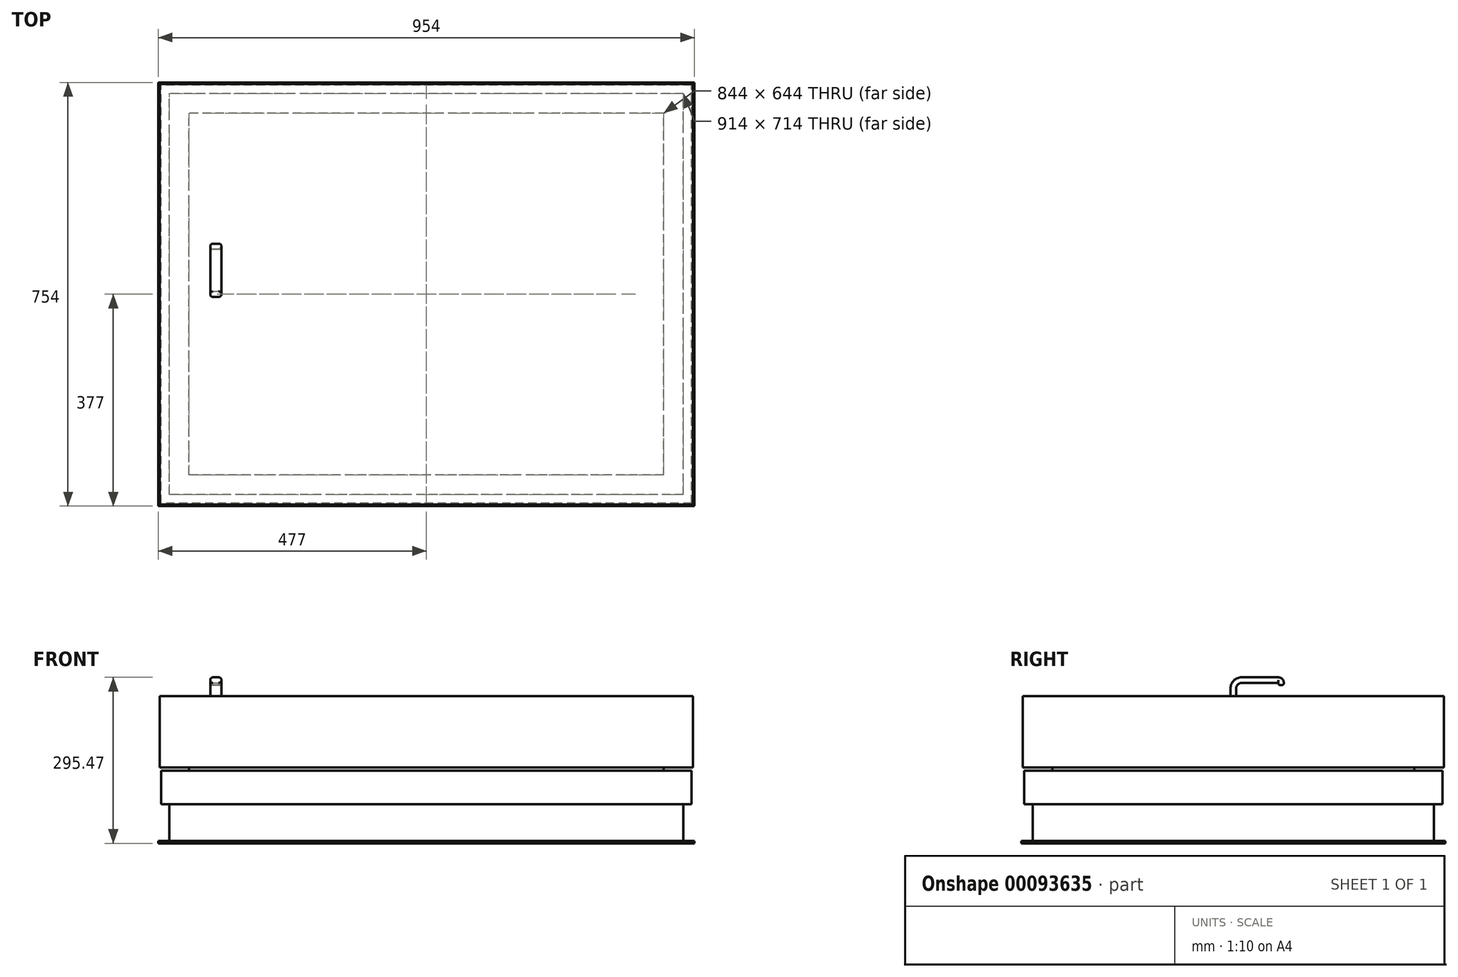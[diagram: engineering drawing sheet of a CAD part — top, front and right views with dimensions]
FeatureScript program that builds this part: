
annotation { "Feature Type Name" : "Feature", "Feature Type Description" : "" }
export const myFeature = defineFeature(function(context is Context, id is Id, definition is map)
    precondition{}
    {
        {
            var Q0;
            Q0=qCreatedBy(makeId("Front.planeOp"),FACE);
            var sketch = newSketch(context, id + "F0", { "sketchPlane" : qUnion([Q0])});
            skLineSegment(sketch, "E0.bottom", {"start": v(-477, -131) * mm, "end": v(477, -131) * mm});
            skLineSegment(sketch, "E0.top", {"start": v(-474.5, 131) * mm, "end": v(474.5, 131) * mm});
            skLineSegment(sketch, "E0.left", {"start": v(-477, -131) * mm, "end": v(-477, -127) * mm});
            skLineSegment(sketch, "E0.right", {"start": v(477, -131) * mm, "end": v(477, -127) * mm});
            skPoint(sketch, "E0.middle", {"position": v(0, 0) * mm});
            skLineSegment(sketch, "E1", {"start": v(477, -127) * mm, "end": v(457, -127) * mm});
            skLineSegment(sketch, "E2", {"start": v(457, -127) * mm, "end": v(457, -61.5) * mm});
            skLineSegment(sketch, "E3", {"start": v(457, -61.5) * mm, "end": v(472, -61.5) * mm});
            skLineSegment(sketch, "E4", {"start": v(472, -61.5) * mm, "end": v(472, -1.5) * mm});
            skLineSegment(sketch, "E5", {"start": v(472, -1.5) * mm, "end": v(422, -1.5) * mm});
            skLineSegment(sketch, "E6", {"start": v(422, -1.5) * mm, "end": v(422, 4) * mm});
            skLineSegment(sketch, "E7", {"start": v(422, 4) * mm, "end": v(474.5, 4) * mm});
            skLineSegment(sketch, "E8", {"start": v(474.5, 4) * mm, "end": v(474.5, 131) * mm});
            skPoint(sketch, "E9.orphan", {"position": v(477, 131) * mm});
            skLineSegment(sketch, "E10.MirrorCS", {"start": v(-474.5, 4) * mm, "end": v(-474.5, 131) * mm});
            skLineSegment(sketch, "E11.MirrorCS", {"start": v(-422, 4) * mm, "end": v(-474.5, 4) * mm});
            skLineSegment(sketch, "E12.MirrorCS", {"start": v(-472, -1.5) * mm, "end": v(-422, -1.5) * mm});
            skLineSegment(sketch, "E13.MirrorCS", {"start": v(-472, -61.5) * mm, "end": v(-472, -1.5) * mm});
            skLineSegment(sketch, "E14.MirrorCS", {"start": v(-457, -127) * mm, "end": v(-457, -61.5) * mm});
            skLineSegment(sketch, "E15.MirrorCS", {"start": v(-457, -61.5) * mm, "end": v(-472, -61.5) * mm});
            skLineSegment(sketch, "E16.MirrorCS", {"start": v(-422, -1.5) * mm, "end": v(-422, 4) * mm});
            skLineSegment(sketch, "E17.MirrorCS", {"start": v(-477, -127) * mm, "end": v(-457, -127) * mm});
            skPoint(sketch, "E18.orphan", {"position": v(-477, 131) * mm});
            skSolve(sketch);
        }
        {
            var Q0;
            Q0 = qSketchRegion(id + "F0", true);
            extrude(context, id + "F1", {"entities" : qUnion([Q0]), "depth" : 754 * mm});
        }
        {
            var Q0;
            Q0=makeQuery(id+"F1.opExtrude","SWEPT_FACE",FACE,{"disambiguationData":[OSD([sQuery(id+"F0.wireOp",EDGE,"E10.MirrorCS")])]});
            var sketch = newSketch(context, id + "F2", { "sketchPlane" : qUnion([Q0])});
            skLineSegment(sketch, "E19.right", {"start": v(754, -131) * mm, "end": v(754, -127) * mm});
            skPoint(sketch, "E19.middle", {"position": v(377, 0) * mm});
            skLineSegment(sketch, "E20", {"start": v(754, -127) * mm, "end": v(734, -127) * mm});
            skLineSegment(sketch, "E21", {"start": v(734, -127) * mm, "end": v(734, -61.5) * mm});
            skLineSegment(sketch, "E22", {"start": v(734, -61.5) * mm, "end": v(749, -61.5) * mm});
            skLineSegment(sketch, "E23", {"start": v(749, -61.5) * mm, "end": v(749, -1.5) * mm});
            skLineSegment(sketch, "E24", {"start": v(749, -1.5) * mm, "end": v(699, -1.5) * mm});
            skLineSegment(sketch, "E25", {"start": v(699, -1.5) * mm, "end": v(699, 4) * mm});
            skLineSegment(sketch, "E26", {"start": v(699, 4) * mm, "end": v(751.5, 4) * mm});
            skLineSegment(sketch, "E27", {"start": v(751.5, 4) * mm, "end": v(751.5, 131) * mm});
            skPoint(sketch, "E28.orphan", {"position": v(754, 131) * mm});
            skPoint(sketch, "E29.orphan", {"position": v(0, 131) * mm});
            skLineSegment(sketch, "E30", {"start": v(377, -206.18) * mm, "end": v(377, 179.39) * mm, "construction": true});
            skPoint(sketch, "E30.startSnap0", {"position": v(377, -131) * mm});
            skPoint(sketch, "E30.endSnap0", {"position": v(377, 131) * mm});
            skLineSegment(sketch, "E31.MirrorCS", {"start": v(2.5, 4) * mm, "end": v(2.5, 131) * mm});
            skLineSegment(sketch, "E32.MirrorCS", {"start": v(55, 4) * mm, "end": v(2.5, 4) * mm});
            skLineSegment(sketch, "E33.MirrorCS", {"start": v(55, -1.5) * mm, "end": v(55, 4) * mm});
            skLineSegment(sketch, "E34.MirrorCS", {"start": v(5, -1.5) * mm, "end": v(55, -1.5) * mm});
            skLineSegment(sketch, "E35.MirrorCS", {"start": v(5, -61.5) * mm, "end": v(5, -1.5) * mm});
            skLineSegment(sketch, "E36.MirrorCS", {"start": v(20, -127) * mm, "end": v(20, -61.5) * mm});
            skLineSegment(sketch, "E37.MirrorCS", {"start": v(20, -61.5) * mm, "end": v(5, -61.5) * mm});
            skLineSegment(sketch, "E38.MirrorCS", {"start": v(0, -127) * mm, "end": v(20, -127) * mm});
            skLineSegment(sketch, "E39.MirrorCS", {"start": v(0, -131) * mm, "end": v(0, -127) * mm});
            skLineSegment(sketch, "E40", {"start": v(751.5, 131) * mm, "end": v(774.44, 131) * mm});
            skLineSegment(sketch, "E41", {"start": v(774.44, 131) * mm, "end": v(765.52, -131) * mm});
            skLineSegment(sketch, "E42", {"start": v(765.52, -131) * mm, "end": v(754, -131) * mm});
            skLineSegment(sketch, "E43.MirrorCS", {"start": v(-20.44, 131) * mm, "end": v(-11.52, -131) * mm});
            skLineSegment(sketch, "E44.MirrorCS", {"start": v(-11.52, -131) * mm, "end": v(0, -131) * mm});
            skLineSegment(sketch, "E45.MirrorCS", {"start": v(2.5, 131) * mm, "end": v(-20.44, 131) * mm});
            skSolve(sketch);
        }
        {
            var Q0;
            Q0 = qSketchRegion(id + "F2", true);
            extrude(context, id + "F3", {"entities" : qUnion([Q0]), "operationType" : NewBodyOperationType.REMOVE, "oppositeDirection" : true, "depth" : 999 * mm});
        }
        {
            var Q0;
            Q0=makeQuery(id+"F1.opExtrude","SWEPT_FACE",FACE,{"disambiguationData":[OSD([sQuery(id+"F0.wireOp",EDGE,"E10.MirrorCS")])]});
            cPlane(context, id + "F4", {"entities" : qUnion([Q0]), "cplaneType" : CPlaneType.OFFSET, "offset" : 100 * mm, "oppositeDirection" : true, "width" : 150 * mm, "height" : 150 * mm});
        }
        {
            var Q0;
            Q0=qCreatedBy(id+"F4.planeOp",FACE);
            var sketch = newSketch(context, id + "F5", { "sketchPlane" : qUnion([Q0])});
            skLineSegment(sketch, "E46", {"start": v(377, 131) * mm, "end": v(377, 144.47) * mm});
            skLineSegment(sketch, "E47", {"start": v(362, 159.47) * mm, "end": v(297, 159.47) * mm});
            skLineSegment(sketch, "E48", {"start": v(292, 154.47) * mm, "end": v(292, 150.87) * mm});
            skPoint(sketch, "E49.visualSharp", {"position": v(377, 159.47) * mm});
            skArc(sketch, "E49.filletArc", {"start": v(377, 144.47) * mm, "mid": v(372.6, 155.08) * mm, "end": v(362, 159.47) * mm});
            skPoint(sketch, "E50.visualSharp", {"position": v(292, 159.47) * mm});
            skArc(sketch, "E50.filletArc", {"start": v(297, 159.47) * mm, "mid": v(293.46, 158) * mm, "end": v(292, 154.47) * mm});
            skSolve(sketch);
        }
        {
            var Q0;
            Q0=makeQuery(id+"F1.opExtrude","SWEPT_FACE",FACE,{"disambiguationData":[OSD([sQuery(id+"F0.wireOp",EDGE,"E0.top")])]});
            var sketch = newSketch(context, id + "F6", { "sketchPlane" : qUnion([Q0])});
            skPoint(sketch, "E51.0", {"position": v(-374.5, -377) * mm});
            skLineSegment(sketch, "E52.bottom", {"start": v(-384.5, -372) * mm, "end": v(-384.5, -382) * mm});
            skLineSegment(sketch, "E52.top", {"start": v(-364.5, -372) * mm, "end": v(-364.5, -382) * mm});
            skLineSegment(sketch, "E52.left", {"start": v(-384.5, -372) * mm, "end": v(-364.5, -372) * mm});
            skLineSegment(sketch, "E52.right", {"start": v(-384.5, -382) * mm, "end": v(-364.5, -382) * mm});
            skSolve(sketch);
        }
        {
            var Q0;
            Q0=makeQuery(id+"F6.imprint","IMPRINT",FACE,{"disambiguationData":[TD([[makeQuery(id+"F6.imprint","IMPRINT",EDGE,{"derivedFrom":sQuery(id+"F6.wireOp",EDGE,"E52.bottom")}),1.0]])]});
            var Q1;
            Q1=sQuery(id+"F5.wireOp",EDGE,"E46");
            var Q2;
            Q2=sQuery(id+"F5.wireOp",EDGE,"E49.filletArc");
            var Q3;
            Q3=sQuery(id+"F5.wireOp",EDGE,"E47");
            var Q4;
            Q4=sQuery(id+"F5.wireOp",EDGE,"E50.filletArc");
            var Q5;
            Q5=sQuery(id+"F5.wireOp",EDGE,"E48");
            sweep(context, id + "F7", {"operationType" : NewBodyOperationType.ADD, "profiles" : qUnion([Q0]), "path" : qUnion([Q1, Q2, Q3, Q4, Q5])});
        }
        {
            var Q0;
            Q0=makeQuery(id+"F7.opSweep","SWEPT_EDGE",EDGE,{"disambiguationData":[OSD([sQuery(id+"F5.wireOp",EDGE,"E47"),sQuery(id+"F6.wireOp",EDGE,"E52.bottom"),sQuery(id+"F6.wireOp",EDGE,"E52.right")])]});
            var Q1;
            Q1=makeQuery(id+"F7.opSweep","SWEPT_EDGE",EDGE,{"disambiguationData":[OSD([sQuery(id+"F5.wireOp",EDGE,"E47"),sQuery(id+"F6.wireOp",EDGE,"E52.bottom"),sQuery(id+"F6.wireOp",EDGE,"E52.left")])]});
            var Q2;
            Q2=makeQuery(id+"F7.opSweep","SWEPT_EDGE",EDGE,{"disambiguationData":[OSD([sQuery(id+"F5.wireOp",EDGE,"E47"),sQuery(id+"F6.wireOp",EDGE,"E52.top"),sQuery(id+"F6.wireOp",EDGE,"E52.right")])]});
            var Q3;
            Q3=makeQuery(id+"F7.opSweep","SWEPT_EDGE",EDGE,{"disambiguationData":[OSD([sQuery(id+"F5.wireOp",EDGE,"E47"),sQuery(id+"F6.wireOp",EDGE,"E52.top"),sQuery(id+"F6.wireOp",EDGE,"E52.left")])]});
            fillet(context, id + "F8", {"entities" : qUnion([Q0, Q1, Q2, Q3]), "radius" : 5 * mm, "tangentPropagation" : true, "allowEdgeOverflow" : false});
        }
        {
            var Q0;
            Q0=makeQuery(id+"F7.opSweep","CAP_EDGE",EDGE,{"disambiguationData":[OSD([sQuery(id+"F5.wireOp",VERTEX,"E48.end"),sQuery(id+"F6.wireOp",EDGE,"E52.right")])],"isStart":false});
            var Q1;
            Q1=makeQuery(id+"F7.opSweep","CAP_EDGE",EDGE,{"disambiguationData":[OSD([sQuery(id+"F5.wireOp",VERTEX,"E48.end"),sQuery(id+"F6.wireOp",EDGE,"E52.left")])],"isStart":false});
            var Q2;
            Q2=makeQuery(id+"F7.opSweep","CAP_EDGE",EDGE,{"disambiguationData":[OSD([sQuery(id+"F5.wireOp",VERTEX,"E48.end"),sQuery(id+"F6.wireOp",EDGE,"E52.bottom")])],"isStart":false});
            fillet(context, id + "F9", {"entities" : qUnion([Q0, Q1, Q2]), "radius" : 3 * mm, "tangentPropagation" : true, "allowEdgeOverflow" : false});
        }
    });
